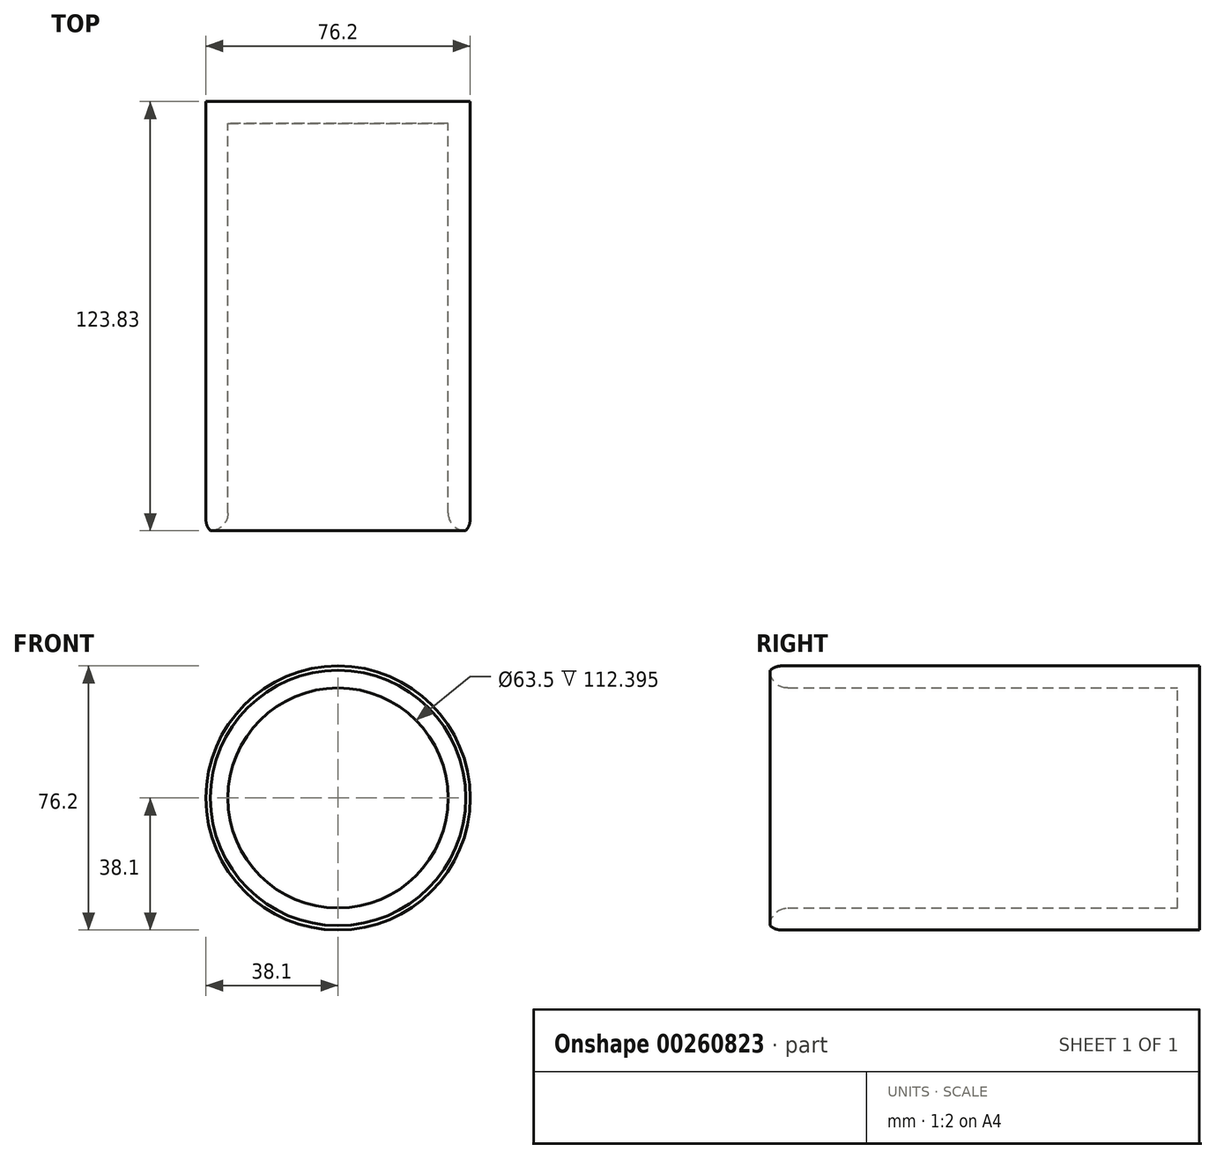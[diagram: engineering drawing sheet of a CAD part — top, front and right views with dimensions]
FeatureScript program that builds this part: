
annotation { "Feature Type Name" : "Feature", "Feature Type Description" : "" }
export const myFeature = defineFeature(function(context is Context, id is Id, definition is map)
    precondition{}
    {
        {
            var Q0;
            Q0=qCreatedBy(makeId("Front.planeOp"),FACE);
            var sketch = newSketch(context, id + "F0", { "sketchPlane" : qUnion([Q0])});
            skCircle(sketch, "E0", {"center": v(0, 0) * mm, "radius": 38.1 * mm});
            skCircle(sketch, "E1", {"center": v(0, 0) * mm, "radius": 31.75 * mm});
            skSolve(sketch);
        }
        {
            var Q0;
            Q0=makeQuery(id+"F0.imprint","IMPRINT",FACE,{"disambiguationData":[TD([[makeQuery(id+"F0.imprint","IMPRINT",EDGE,{"derivedFrom":sQuery(id+"F0.wireOp",EDGE,"E0")}),1.0]])]});
            extrude(context, id + "F1", {"entities" : qUnion([Q0]), "depth" : 123.82 * mm});
        }
        {
            var Q0;
            Q0=qCreatedBy(makeId("Front.planeOp"),FACE);
            var sketch = newSketch(context, id + "F2", { "sketchPlane" : qUnion([Q0])});
            skCircle(sketch, "E2", {"center": v(0, 0) * mm, "radius": 38.1 * mm});
            skSolve(sketch);
        }
        {
            var Q0;
            Q0 = qSketchRegion(id + "F2", true);
            extrude(context, id + "F3", {"entities" : qUnion([Q0]), "operationType" : NewBodyOperationType.ADD, "depth" : 6.35 * mm});
        }
        {
            var Q0;
            Q0=makeQuery(id+"F1.opExtrude","CAP_EDGE",EDGE,{"disambiguationData":[OSD([sQuery(id+"F0.wireOp",EDGE,"E1")])],"isStart":false});
            fillet(context, id + "F4", {"entities" : qUnion([Q0]), "radius" : 5.08 * mm, "tangentPropagation" : true, "allowEdgeOverflow" : false});
        }
        {
            var Q0;
            Q0=makeQuery(id+"F1.opExtrude","CAP_EDGE",EDGE,{"disambiguationData":[OSD([sQuery(id+"F0.wireOp",EDGE,"E0")])],"isStart":false});
            fillet(context, id + "F5", {"entities" : qUnion([Q0]), "radius" : 5.08 * mm, "tangentPropagation" : true, "allowEdgeOverflow" : false});
        }
    });
